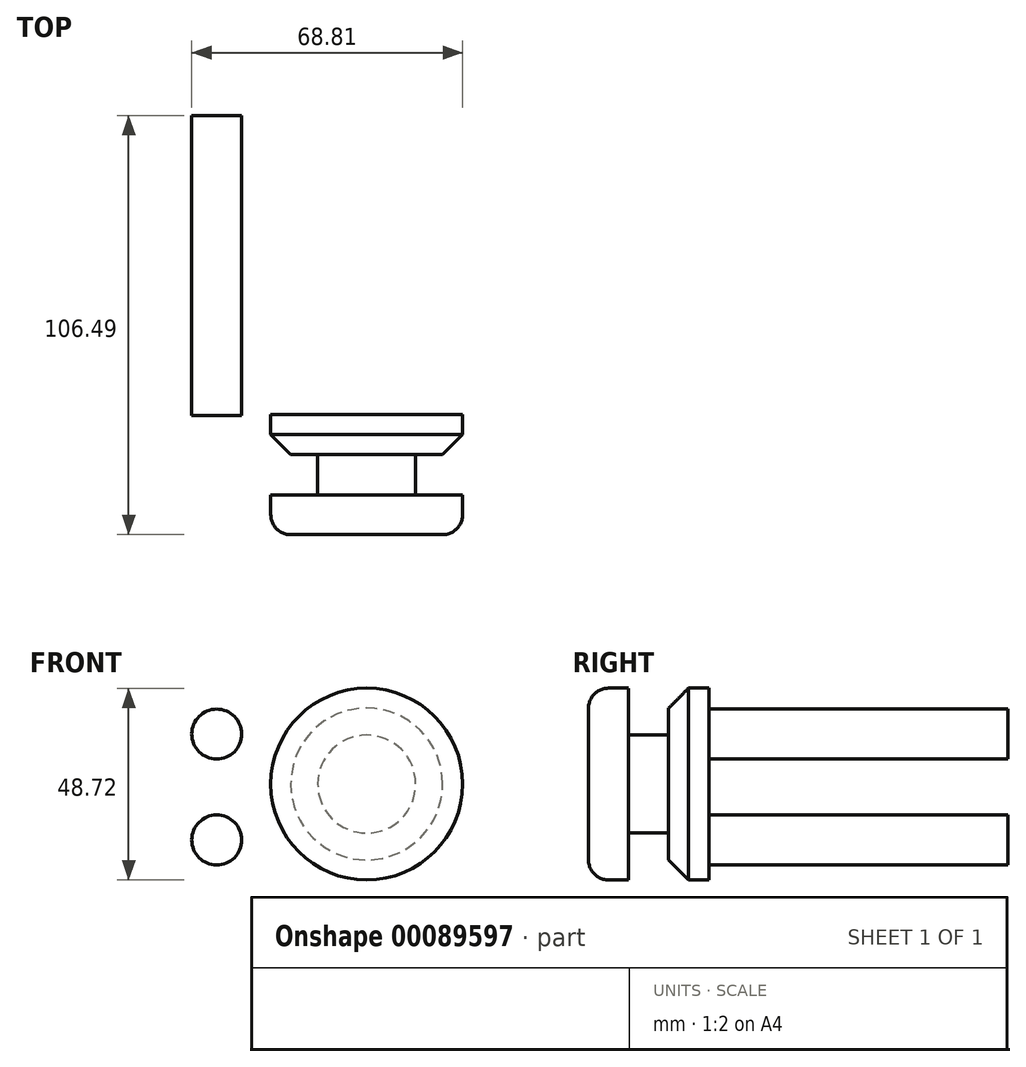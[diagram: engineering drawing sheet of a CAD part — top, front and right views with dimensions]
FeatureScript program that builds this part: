
annotation { "Feature Type Name" : "Feature", "Feature Type Description" : "" }
export const myFeature = defineFeature(function(context is Context, id is Id, definition is map)
    precondition{}
    {
        {
            var Q0;
            Q0=qCreatedBy(makeId("Front.planeOp"),FACE);
            var sketch = newSketch(context, id + "F0", { "sketchPlane" : qUnion([Q0])});
            skLineSegment(sketch, "E0", {"start": v(-50.8, 25.4) * mm, "end": v(50.8, 25.4) * mm});
            skLineSegment(sketch, "E1", {"start": v(50.8, 25.4) * mm, "end": v(50.8, -25.4) * mm});
            skLineSegment(sketch, "E2", {"start": v(50.8, -25.4) * mm, "end": v(-50.8, -25.4) * mm});
            skLineSegment(sketch, "E3", {"start": v(-50.8, -25.4) * mm, "end": v(-50.8, 25.4) * mm});
            skSolve(sketch);
        }
        {
            var Q0;
            Q0=makeQuery(id+"F0.imprint","IMPRINT",FACE,{"disambiguationData":[TD([[makeQuery(id+"F0.imprint","IMPRINT",EDGE,{"derivedFrom":sQuery(id+"F0.wireOp",EDGE,"E0")}),-1.0]])]});
            extrude(context, id + "F1", {"entities" : qUnion([Q0]), "depth" : 76.2 * mm});
        }
        {
            var Q0;
            Q0=makeQuery(id+"F1.opExtrude","CAP_FACE",FACE,{"disambiguationData":[OSD([sQuery(id+"F0.wireOp",EDGE,"E0"),sQuery(id+"F0.wireOp",EDGE,"E1"),sQuery(id+"F0.wireOp",EDGE,"E2"),sQuery(id+"F0.wireOp",EDGE,"E3")])],"isStart":true});
            var sketch = newSketch(context, id + "F2", { "sketchPlane" : qUnion([Q0])});
            skCircle(sketch, "E4", {"center": v(-38.1, 12.7) * mm, "radius": 6.35 * mm});
            skCircle(sketch, "E5", {"center": v(-38.1, -14.2) * mm, "radius": 6.35 * mm});
            skLineSegment(sketch, "E6", {"start": v(0, 46.8) * mm, "end": v(0, -35.54) * mm, "construction": true});
            skPoint(sketch, "E6.endSnap0", {"position": v(0, 25.4) * mm});
            skCircle(sketch, "E7.MirrorC", {"center": v(38.1, -14.2) * mm, "radius": 6.35 * mm});
            skCircle(sketch, "E8.MirrorC", {"center": v(38.1, 12.7) * mm, "radius": 6.35 * mm});
            skSolve(sketch);
        }
        {
            var Q0;
            Q0=makeQuery(id+"F2.imprint","IMPRINT",FACE,{"disambiguationData":[TD([[makeQuery(id+"F2.imprint","IMPRINT",EDGE,{"derivedFrom":sQuery(id+"F2.wireOp",EDGE,"E4")}),1.0]])]});
            var Q1;
            Q1=makeQuery(id+"F2.imprint","IMPRINT",FACE,{"disambiguationData":[TD([[makeQuery(id+"F2.imprint","IMPRINT",EDGE,{"derivedFrom":sQuery(id+"F2.wireOp",EDGE,"E8.MirrorC")}),-1.0]])]});
            var Q2;
            Q2=makeQuery(id+"F2.imprint","IMPRINT",FACE,{"disambiguationData":[TD([[makeQuery(id+"F2.imprint","IMPRINT",EDGE,{"derivedFrom":sQuery(id+"F2.wireOp",EDGE,"E5")}),1.0]])]});
            var Q3;
            Q3=makeQuery(id+"F2.imprint","IMPRINT",FACE,{"disambiguationData":[TD([[makeQuery(id+"F2.imprint","IMPRINT",EDGE,{"derivedFrom":sQuery(id+"F2.wireOp",EDGE,"E7.MirrorC")}),-1.0]])]});
            extrude(context, id + "F3", {"entities" : qUnion([Q0, Q1, Q2, Q3]), "operationType" : NewBodyOperationType.REMOVE, "endBound" : BoundingType.THROUGH_ALL, "oppositeDirection" : true, "depth" : 25.4 * mm});
        }
        {
            var Q0;
            Q0=qCreatedBy(makeId("Top.planeOp"),FACE);
            var sketch = newSketch(context, id + "F4", { "sketchPlane" : qUnion([Q0])});
            skLineSegment(sketch, "E9", {"start": v(-24.36, -106.49) * mm, "end": v(-24.36, -75.94) * mm});
            skLineSegment(sketch, "E10", {"start": v(-24.36, -106.49) * mm, "end": v(0, -106.49) * mm});
            skLineSegment(sketch, "E11", {"start": v(0, -106.49) * mm, "end": v(0, -75.94) * mm});
            skLineSegment(sketch, "E12", {"start": v(0, -75.94) * mm, "end": v(-24.36, -75.94) * mm});
            skLineSegment(sketch, "E13", {"start": v(0, -160.4) * mm, "end": v(0, 14.12) * mm, "construction": true});
            skSolve(sketch);
        }
        {
            var Q0;
            Q0=makeQuery(id+"F4.imprint","IMPRINT",FACE,{"disambiguationData":[TD([[makeQuery(id+"F4.imprint","IMPRINT",EDGE,{"derivedFrom":sQuery(id+"F4.wireOp",EDGE,"E9")}),-1.0]])]});
            var Q1;
            Q1=sQuery(id+"F4.wireOp",EDGE,"E13");
            revolve(context, id + "F5", {"operationType" : NewBodyOperationType.ADD, "entities" : qUnion([Q0]), "axis" : qUnion([Q1]), "revolveType" : RevolveType.FULL});
        }
        {
            var Q0;
            Q0=qCreatedBy(makeId("Top.planeOp"),FACE);
            var sketch = newSketch(context, id + "F6", { "sketchPlane" : qUnion([Q0])});
            skLineSegment(sketch, "E14", {"start": v(-24.36, -96.37) * mm, "end": v(-24.36, -86.16) * mm});
            skLineSegment(sketch, "E15", {"start": v(-24.36, -96.37) * mm, "end": v(-12.45, -96.37) * mm});
            skLineSegment(sketch, "E16", {"start": v(-12.45, -96.37) * mm, "end": v(-12.45, -86.16) * mm});
            skLineSegment(sketch, "E17", {"start": v(-12.45, -86.16) * mm, "end": v(-24.36, -86.16) * mm});
            skLineSegment(sketch, "E18", {"start": v(0, -111.44) * mm, "end": v(0, -50.48) * mm, "construction": true});
            skSolve(sketch);
        }
        {
            var Q0;
            Q0=makeQuery(id+"F6.imprint","IMPRINT",FACE,{"disambiguationData":[TD([[makeQuery(id+"F6.imprint","IMPRINT",EDGE,{"derivedFrom":sQuery(id+"F6.wireOp",EDGE,"E14")}),-1.0]])]});
            var Q1;
            Q1=sQuery(id+"F6.wireOp",EDGE,"E18");
            revolve(context, id + "F7", {"operationType" : NewBodyOperationType.REMOVE, "entities" : qUnion([Q0]), "axis" : qUnion([Q1]), "revolveType" : RevolveType.FULL, "oppositeDirection" : true});
        }
        {
            var Q0;
            Q0=makeQuery(id+"F5.opRevolve","SWEPT_EDGE",EDGE,{"disambiguationData":[OSD([sQuery(id+"F4.wireOp",EDGE,"E9"),sQuery(id+"F4.wireOp",EDGE,"E10")])]});
            fillet(context, id + "F8", {"entities" : qUnion([Q0]), "radius" : 5.08 * mm, "tangentPropagation" : true, "allowEdgeOverflow" : false});
        }
        {
            var Q0;
            Q0=makeQuery(id+"F7.boolean.opBoolean","COPY",EDGE,{"derivedFrom":makeQuery(id+"F7.opRevolve","SWEPT_EDGE",EDGE,{"disambiguationData":[OSD([sQuery(id+"F6.wireOp",EDGE,"E14"),sQuery(id+"F6.wireOp",EDGE,"E17")])]})});
            chamfer(context, id + "F9", {"entities" : qUnion([Q0]), "width" : 5.08 * mm, "tangentPropagation" : true});
        }
    });
